# Revit family: NaughtOne_SymbolTwoSeatLounge
name_source: partatom
category: Furniture
units: mm (PartAtom-declared; Revit-internal decimal feet)

## family parameters
Always vertical = Yes
Cut with Voids When Loaded = No
Enable Cutting in Views = No
OmniClass Number = 23.40.20.00
OmniClass Title = General Furniture and Specialties
Render Appearance Source = Family Geometry
Room Calculation Point = No
Shared = Yes
Work Plane-Based = No

## types (1)
- Seat Bench Single Fabric Lounge Ht
    Assembly Code = E2020200
    Default Elevation = 0 "
    Description = Symbol Two Seat Bench lounge height 16 inch seat height Single Fabric
    Foot aux 1 = 9.634 "
    Foot aux 2 = 19.55 "
    Manufacturer = Herman Miller, Inc.
    Model = NOSYN210L1
    Package Qty = 1
    Seat Aux 1 = 25 "
    Seat Aux 2 = 25 "
    Seat Bench Single Fabric = Yes
    Seat Left Arm Single and Multiple Fabric = No
    Seat No Arms Single and Multiple Fabric = No
    Seat Right Arm Single and Multiple Fabric = No
    Seat Two Arms Single and Multiple Fabric = No
    Type = 1
    URL = http://www.hermanmiller.com

## geometry (parser evidence)
native form markers: Sweep x6
no freeform markers — native parametric forms only
